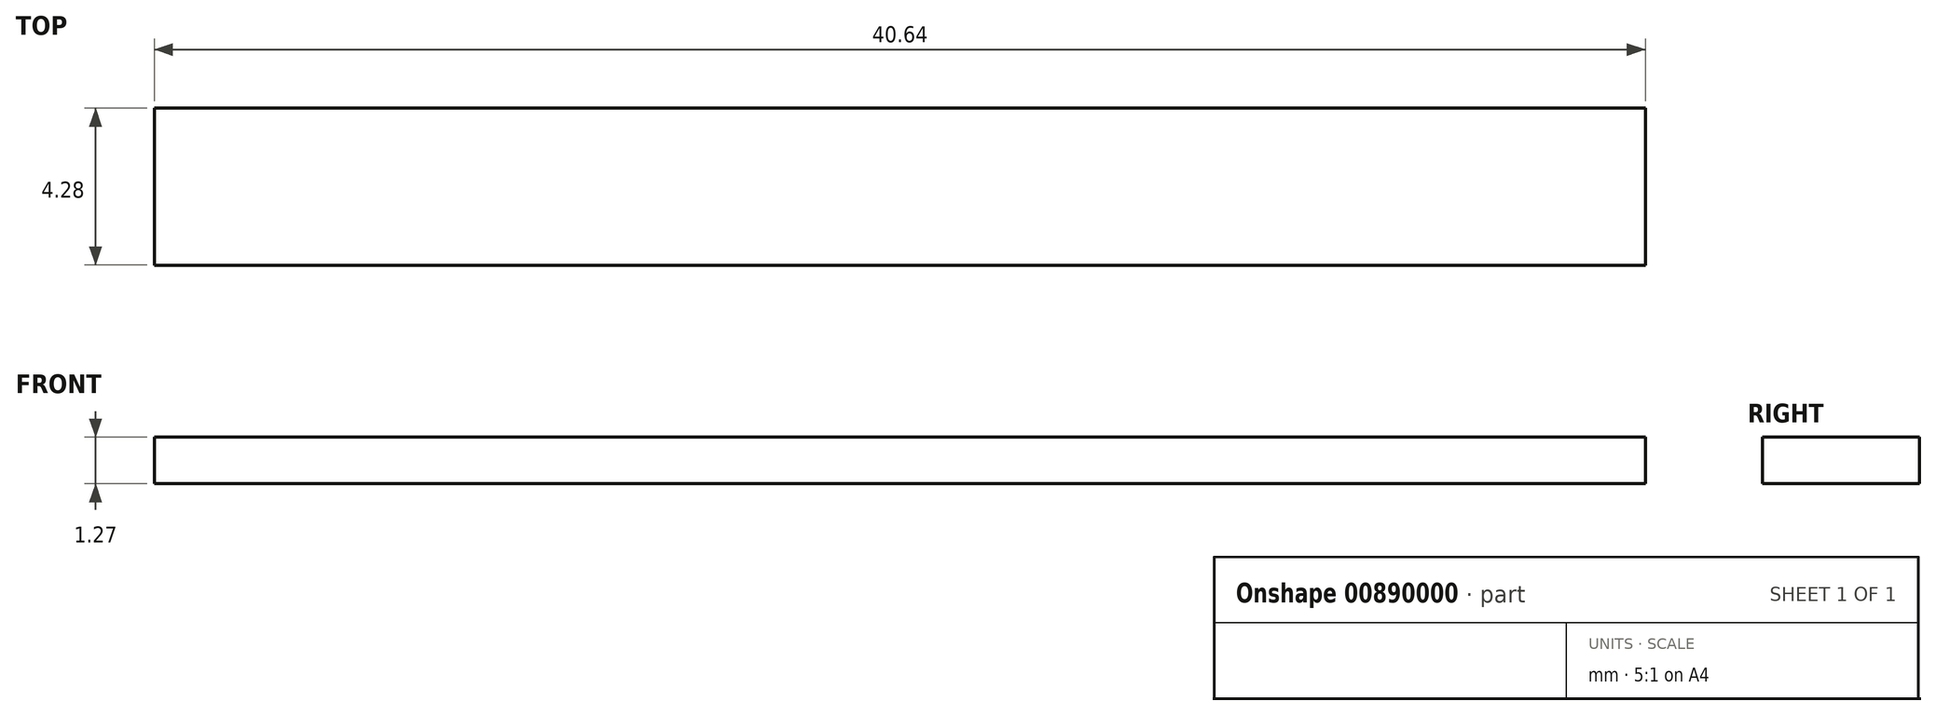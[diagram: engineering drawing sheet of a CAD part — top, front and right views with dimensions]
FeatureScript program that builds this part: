
annotation { "Feature Type Name" : "Feature", "Feature Type Description" : "" }
export const myFeature = defineFeature(function(context is Context, id is Id, definition is map)
    precondition{}
    {
        {
            var Q0;
            Q0=qCreatedBy(makeId("Top.planeOp"),FACE);
            var sketch = newSketch(context, id + "F0", { "sketchPlane" : qUnion([Q0])});
            skLineSegment(sketch, "E0", {"start": v(-20.96, -37.8) * mm, "end": v(19.68, -37.8) * mm});
            skLineSegment(sketch, "E1.bottom", {"start": v(-20.96, -16.06) * mm, "end": v(19.68, -16.06) * mm});
            skLineSegment(sketch, "E1.top", {"start": v(-20.96, -20.34) * mm, "end": v(19.68, -20.34) * mm});
            skLineSegment(sketch, "E1.left", {"start": v(-20.96, -16.06) * mm, "end": v(-20.96, -20.34) * mm});
            skLineSegment(sketch, "E1.right", {"start": v(19.68, -16.06) * mm, "end": v(19.68, -20.34) * mm});
            skSolve(sketch);
        }
        {
            var Q0;
            Q0=makeQuery(id+"F0.imprint","IMPRINT",FACE,{"disambiguationData":[TD([[makeQuery(id+"F0.imprint","IMPRINT",EDGE,{"derivedFrom":sQuery(id+"F0.wireOp",EDGE,"E1.bottom")}),-1.0]])]});
            extrude(context, id + "F1", {"entities" : qUnion([Q0]), "depth" : 1.27 * mm, "offsetDistance" : 25.4 * mm});
        }
    });
